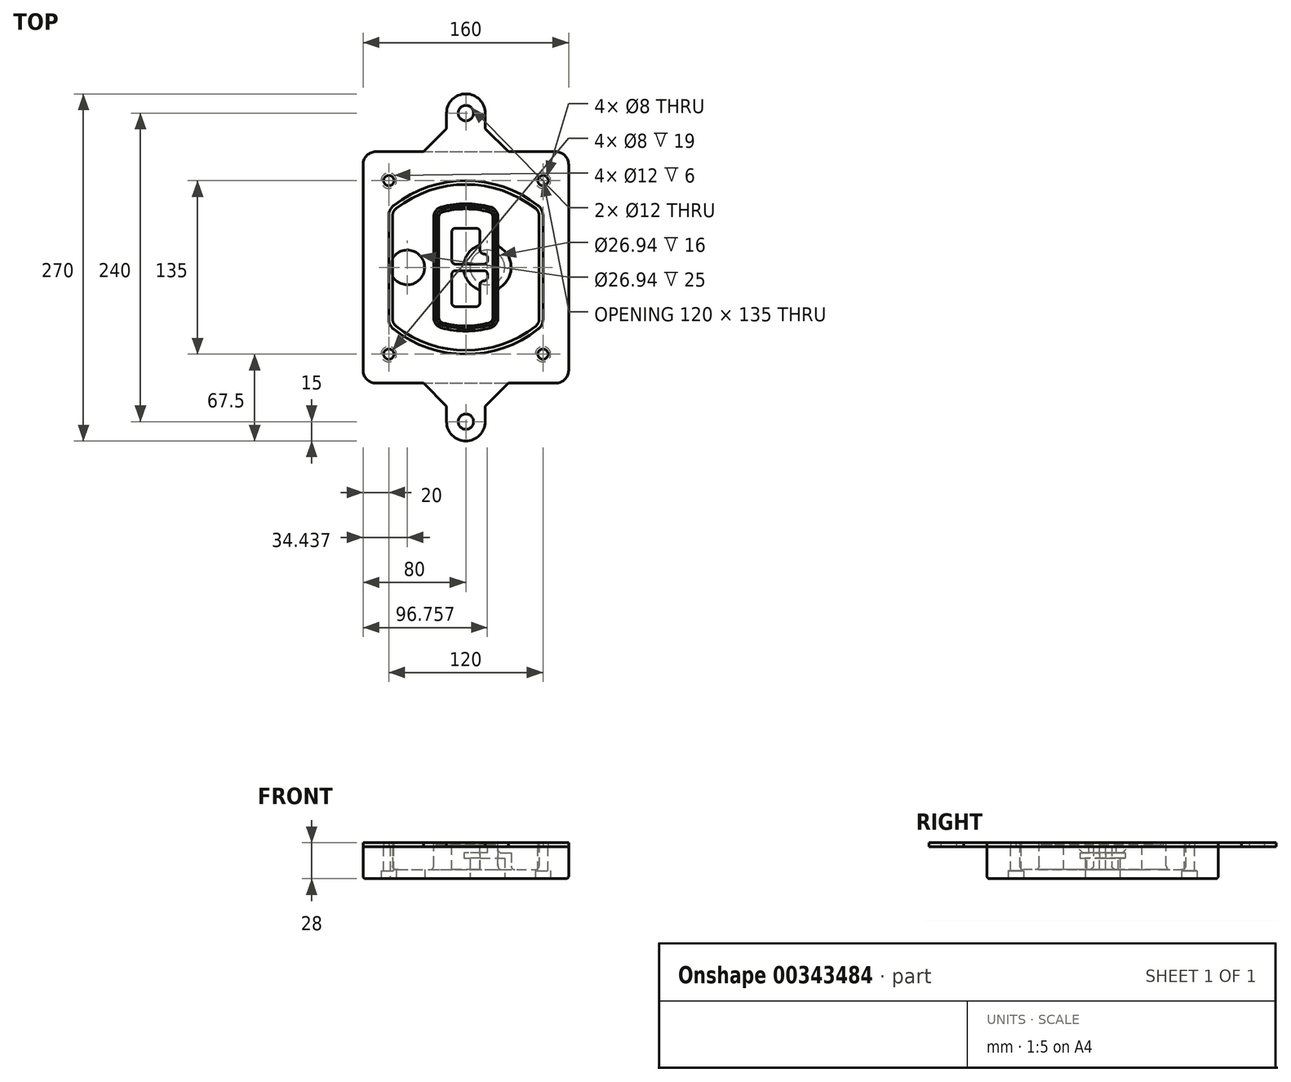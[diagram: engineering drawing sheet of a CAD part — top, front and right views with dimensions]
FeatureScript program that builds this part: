
annotation { "Feature Type Name" : "Feature", "Feature Type Description" : "" }
export const myFeature = defineFeature(function(context is Context, id is Id, definition is map)
    precondition{}
    {
        {
            var Q0;
            Q0=qCreatedBy(makeId("Top.planeOp"),FACE);
            var sketch = newSketch(context, id + "F0", { "sketchPlane" : qUnion([Q0])});
            skPoint(sketch, "E0.rect.middle", {"position": v(0, 0) * mm});
            skLineSegment(sketch, "E1.bottom", {"start": v(-70, -90) * mm, "end": v(70, -90) * mm});
            skLineSegment(sketch, "E1.top", {"start": v(-70, 90) * mm, "end": v(70, 90) * mm});
            skLineSegment(sketch, "E1.left", {"start": v(-80, -80) * mm, "end": v(-80, 80) * mm});
            skLineSegment(sketch, "E1.right", {"start": v(80, -80) * mm, "end": v(80, 80) * mm});
            skLineSegment(sketch, "E2", {"start": v(-80, 90) * mm, "end": v(80, -90) * mm, "construction": true});
            skLineSegment(sketch, "E3", {"start": v(80, 90) * mm, "end": v(-80, -90) * mm, "construction": true});
            skCircle(sketch, "E4", {"center": v(-60, 67.5) * mm, "radius": 4 * mm});
            skCircle(sketch, "E5", {"center": v(60, 67.5) * mm, "radius": 4 * mm});
            skCircle(sketch, "E6", {"center": v(60, -67.5) * mm, "radius": 4 * mm});
            skCircle(sketch, "E7", {"center": v(-60, -67.5) * mm, "radius": 4 * mm});
            skLineSegment(sketch, "E8", {"start": v(-60, 67.5) * mm, "end": v(60, 67.5) * mm, "construction": true});
            skLineSegment(sketch, "E9", {"start": v(60, 67.5) * mm, "end": v(60, -67.5) * mm, "construction": true});
            skLineSegment(sketch, "E10", {"start": v(60, -67.5) * mm, "end": v(-60, -67.5) * mm, "construction": true});
            skLineSegment(sketch, "E11", {"start": v(-60, -67.5) * mm, "end": v(-60, 67.5) * mm, "construction": true});
            skLineSegment(sketch, "E12", {"start": v(-60, 40.3) * mm, "end": v(-60, -40.3) * mm});
            skLineSegment(sketch, "E13", {"start": v(60, 40.3) * mm, "end": v(60, -40.3) * mm});
            skArc(sketch, "E14", {"start": v(56.15, 48.18) * mm, "mid": v(0, 67.5) * mm, "end": v(-56.15, 48.18) * mm});
            skArc(sketch, "E15", {"start": v(-56.15, -48.18) * mm, "mid": v(0, -67.5) * mm, "end": v(56.15, -48.18) * mm});
            skLineSegment(sketch, "E16", {"start": v(-60, 0) * mm, "end": v(60, 0) * mm, "construction": true});
            skPoint(sketch, "E17.visualSharp", {"position": v(-60, -45) * mm});
            skArc(sketch, "E17.filletArc", {"start": v(-60, -40.3) * mm, "mid": v(-58.99, -44.68) * mm, "end": v(-56.15, -48.18) * mm});
            skPoint(sketch, "E18.visualSharp", {"position": v(-60, 45) * mm});
            skArc(sketch, "E18.filletArc", {"start": v(-56.15, 48.18) * mm, "mid": v(-58.99, 44.68) * mm, "end": v(-60, 40.3) * mm});
            skPoint(sketch, "E19.visualSharp", {"position": v(60, 45) * mm});
            skArc(sketch, "E19.filletArc", {"start": v(60, 40.3) * mm, "mid": v(58.99, 44.68) * mm, "end": v(56.15, 48.18) * mm});
            skPoint(sketch, "E20.visualSharp", {"position": v(60, -45) * mm});
            skArc(sketch, "E20.filletArc", {"start": v(56.15, -48.18) * mm, "mid": v(58.99, -44.68) * mm, "end": v(60, -40.3) * mm});
            skPoint(sketch, "E21.visualSharp", {"position": v(-80, 90) * mm});
            skArc(sketch, "E21.filletArc", {"start": v(-70, 90) * mm, "mid": v(-77.07, 87.07) * mm, "end": v(-80, 80) * mm});
            skPoint(sketch, "E22.visualSharp", {"position": v(80, 90) * mm});
            skArc(sketch, "E22.filletArc", {"start": v(80, 80) * mm, "mid": v(77.07, 87.07) * mm, "end": v(70, 90) * mm});
            skPoint(sketch, "E23.visualSharp", {"position": v(80, -90) * mm});
            skArc(sketch, "E23.filletArc", {"start": v(70, -90) * mm, "mid": v(77.07, -87.07) * mm, "end": v(80, -80) * mm});
            skPoint(sketch, "E24.visualSharp", {"position": v(-80, -90) * mm});
            skArc(sketch, "E24.filletArc", {"start": v(-80, -80) * mm, "mid": v(-77.07, -87.07) * mm, "end": v(-70, -90) * mm});
            skArc(sketch, "E25.0", {"start": v(57, 40.3) * mm, "mid": v(56.3, 43.36) * mm, "end": v(54.3, 45.81) * mm});
            skLineSegment(sketch, "E25.1", {"start": v(57, 40.3) * mm, "end": v(57, -40.3) * mm});
            skArc(sketch, "E25.2", {"start": v(54.3, -45.81) * mm, "mid": v(56.3, -43.36) * mm, "end": v(57, -40.3) * mm});
            skArc(sketch, "E25.3", {"start": v(-54.3, -45.81) * mm, "mid": v(0, -64.5) * mm, "end": v(54.3, -45.81) * mm});
            skArc(sketch, "E25.4", {"start": v(-57, -40.3) * mm, "mid": v(-56.3, -43.36) * mm, "end": v(-54.3, -45.81) * mm});
            skArc(sketch, "E25.5", {"start": v(54.3, 45.81) * mm, "mid": v(0, 64.5) * mm, "end": v(-54.3, 45.81) * mm});
            skLineSegment(sketch, "E25.6", {"start": v(-57, 40.3) * mm, "end": v(-57, -40.3) * mm});
            skArc(sketch, "E25.7", {"start": v(-54.3, 45.81) * mm, "mid": v(-56.3, 43.36) * mm, "end": v(-57, 40.3) * mm});
            skArc(sketch, "E26.0", {"start": v(-58.62, 51.33) * mm, "mid": v(-62.58, 46.43) * mm, "end": v(-64, 40.3) * mm});
            skArc(sketch, "E26.1", {"start": v(58.62, 51.33) * mm, "mid": v(0, 71.5) * mm, "end": v(-58.62, 51.33) * mm});
            skArc(sketch, "E26.2", {"start": v(64, 40.3) * mm, "mid": v(62.58, 46.43) * mm, "end": v(58.62, 51.33) * mm});
            skLineSegment(sketch, "E26.3", {"start": v(64, 40.3) * mm, "end": v(64, -40.3) * mm});
            skArc(sketch, "E26.4", {"start": v(58.62, -51.33) * mm, "mid": v(62.58, -46.43) * mm, "end": v(64, -40.3) * mm});
            skLineSegment(sketch, "E26.5", {"start": v(-64, 40.3) * mm, "end": v(-64, -40.3) * mm});
            skArc(sketch, "E26.6", {"start": v(-58.62, -51.33) * mm, "mid": v(0, -71.5) * mm, "end": v(58.62, -51.33) * mm});
            skArc(sketch, "E26.7", {"start": v(-64, -40.3) * mm, "mid": v(-62.58, -46.43) * mm, "end": v(-58.62, -51.33) * mm});
            skSolve(sketch);
        }
        {
            var Q0;
            Q0=makeQuery(id+"F0.imprint","IMPRINT",FACE,{"disambiguationData":[TD([[makeQuery(id+"F0.imprint","IMPRINT",EDGE,{"derivedFrom":sQuery(id+"F0.wireOp",EDGE,"E1.bottom")}),1.0]])]});
            var Q1;
            Q1=makeQuery(id+"F0.imprint","IMPRINT",FACE,{"disambiguationData":[TD([[makeQuery(id+"F0.imprint","IMPRINT",EDGE,{"derivedFrom":sQuery(id+"F0.wireOp",EDGE,"E12")}),1.0]])]});
            var Q2;
            Q2=makeQuery(id+"F0.imprint","IMPRINT",FACE,{"disambiguationData":[TD([[makeQuery(id+"F0.imprint","IMPRINT",EDGE,{"derivedFrom":sQuery(id+"F0.wireOp",EDGE,"E25.0")}),1.0]])]});
            var Q3;
            Q3=makeQuery(id+"F0.imprint","IMPRINT",FACE,{"disambiguationData":[TD([[makeQuery(id+"F0.imprint","IMPRINT",EDGE,{"derivedFrom":sQuery(id+"F0.wireOp",EDGE,"E12")}),-1.0]])]});
            extrude(context, id + "F1", {"entities" : qUnion([Q0, Q1, Q2, Q3]), "oppositeDirection" : true, "depth" : 25 * mm});
        }
        {
            var Q0;
            Q0=makeQuery(id+"F0.imprint","IMPRINT",FACE,{"disambiguationData":[TD([[makeQuery(id+"F0.imprint","IMPRINT",EDGE,{"derivedFrom":sQuery(id+"F0.wireOp",EDGE,"E12")}),1.0]])]});
            extrude(context, id + "F2", {"entities" : qUnion([Q0]), "operationType" : NewBodyOperationType.ADD, "depth" : 3 * mm});
        }
        {
            var Q0;
            Q0=makeQuery(id+"F0.imprint","IMPRINT",FACE,{"disambiguationData":[TD([[makeQuery(id+"F0.imprint","IMPRINT",EDGE,{"derivedFrom":sQuery(id+"F0.wireOp",EDGE,"E25.0")}),1.0]])]});
            extrude(context, id + "F3", {"entities" : qUnion([Q0]), "operationType" : NewBodyOperationType.REMOVE, "oppositeDirection" : true, "depth" : 18 * mm});
        }
        {
            var Q0;
            Q0=makeQuery(id+"F2.opExtrude","CAP_FACE",FACE,{"disambiguationData":[OSD([sQuery(id+"F0.wireOp",EDGE,"E12"),sQuery(id+"F0.wireOp",EDGE,"E13"),sQuery(id+"F0.wireOp",EDGE,"E14"),sQuery(id+"F0.wireOp",EDGE,"E15"),sQuery(id+"F0.wireOp",EDGE,"E17.filletArc"),sQuery(id+"F0.wireOp",EDGE,"E18.filletArc"),sQuery(id+"F0.wireOp",EDGE,"E19.filletArc"),sQuery(id+"F0.wireOp",EDGE,"E20.filletArc"),sQuery(id+"F0.wireOp",EDGE,"E25.0"),sQuery(id+"F0.wireOp",EDGE,"E25.1"),sQuery(id+"F0.wireOp",EDGE,"E25.2"),sQuery(id+"F0.wireOp",EDGE,"E25.3"),sQuery(id+"F0.wireOp",EDGE,"E25.4"),sQuery(id+"F0.wireOp",EDGE,"E25.5"),sQuery(id+"F0.wireOp",EDGE,"E25.6"),sQuery(id+"F0.wireOp",EDGE,"E25.7")])],"isStart":false});
            var sketch = newSketch(context, id + "F4", { "sketchPlane" : qUnion([Q0])});
            skArc(sketch, "E27.0", {"start": v(-19.08, -46.97) * mm, "mid": v(0, -49.5) * mm, "end": v(19.08, -46.97) * mm});
            skArc(sketch, "E28.0", {"start": v(19.08, 46.97) * mm, "mid": v(0, 49.5) * mm, "end": v(-19.08, 46.97) * mm});
            skLineSegment(sketch, "E29", {"start": v(-25, 39.25) * mm, "end": v(-25, -39.25) * mm});
            skLineSegment(sketch, "E30", {"start": v(25, 39.25) * mm, "end": v(25, -39.25) * mm});
            skLineSegment(sketch, "E31", {"start": v(-25, 45.1) * mm, "end": v(25, 45.1) * mm, "construction": true});
            skLineSegment(sketch, "E32", {"start": v(-25, -45.1) * mm, "end": v(25, -45.1) * mm, "construction": true});
            skPoint(sketch, "E33.visualSharp", {"position": v(-25, 45.1) * mm});
            skArc(sketch, "E33.filletArc", {"start": v(-19.08, 46.97) * mm, "mid": v(-23.35, 44.11) * mm, "end": v(-25, 39.25) * mm});
            skPoint(sketch, "E34.visualSharp", {"position": v(25, 45.1) * mm});
            skArc(sketch, "E34.filletArc", {"start": v(25, 39.25) * mm, "mid": v(23.35, 44.11) * mm, "end": v(19.08, 46.97) * mm});
            skPoint(sketch, "E35.visualSharp", {"position": v(25, -45.1) * mm});
            skArc(sketch, "E35.filletArc", {"start": v(19.08, -46.97) * mm, "mid": v(23.35, -44.11) * mm, "end": v(25, -39.25) * mm});
            skPoint(sketch, "E36.visualSharp", {"position": v(-25, -45.1) * mm});
            skArc(sketch, "E36.filletArc", {"start": v(-25, -39.25) * mm, "mid": v(-23.35, -44.11) * mm, "end": v(-19.08, -46.97) * mm});
            skArc(sketch, "E37.0", {"start": v(54.3, 45.81) * mm, "mid": v(0, 64.5) * mm, "end": v(-54.3, 45.81) * mm});
            skArc(sketch, "E37.1", {"start": v(-54.3, 45.81) * mm, "mid": v(-56.3, 43.36) * mm, "end": v(-57, 40.3) * mm});
            skLineSegment(sketch, "E37.2", {"start": v(-57, 40.3) * mm, "end": v(-57, -40.3) * mm});
            skArc(sketch, "E37.3", {"start": v(-57, -40.3) * mm, "mid": v(-56.3, -43.36) * mm, "end": v(-54.3, -45.81) * mm});
            skArc(sketch, "E37.4", {"start": v(-54.3, -45.81) * mm, "mid": v(0, -64.5) * mm, "end": v(54.3, -45.81) * mm});
            skArc(sketch, "E37.5", {"start": v(54.3, -45.81) * mm, "mid": v(56.3, -43.36) * mm, "end": v(57, -40.3) * mm});
            skLineSegment(sketch, "E37.6", {"start": v(57, 40.3) * mm, "end": v(57, -40.3) * mm});
            skArc(sketch, "E37.7", {"start": v(57, 40.3) * mm, "mid": v(56.3, 43.36) * mm, "end": v(54.3, 45.81) * mm});
            skLineSegment(sketch, "E38.0", {"start": v(23, 39.25) * mm, "end": v(23, -39.25) * mm});
            skArc(sketch, "E38.1", {"start": v(18.56, -45.04) * mm, "mid": v(21.76, -42.9) * mm, "end": v(23, -39.25) * mm});
            skArc(sketch, "E38.2", {"start": v(-18.56, -45.04) * mm, "mid": v(0, -47.5) * mm, "end": v(18.56, -45.04) * mm});
            skArc(sketch, "E38.3", {"start": v(-23, -39.25) * mm, "mid": v(-21.76, -42.9) * mm, "end": v(-18.56, -45.04) * mm});
            skLineSegment(sketch, "E38.4", {"start": v(-23, 39.25) * mm, "end": v(-23, -39.25) * mm});
            skArc(sketch, "E38.5", {"start": v(23, 39.25) * mm, "mid": v(21.76, 42.9) * mm, "end": v(18.56, 45.04) * mm});
            skArc(sketch, "E38.6", {"start": v(-18.56, 45.04) * mm, "mid": v(-21.76, 42.9) * mm, "end": v(-23, 39.25) * mm});
            skArc(sketch, "E38.7", {"start": v(18.56, 45.04) * mm, "mid": v(0, 47.5) * mm, "end": v(-18.56, 45.04) * mm});
            skArc(sketch, "E39.0", {"start": v(21, 39.25) * mm, "mid": v(20.18, 41.68) * mm, "end": v(18.04, 43.1) * mm});
            skLineSegment(sketch, "E39.1", {"start": v(21, 39.25) * mm, "end": v(21, -39.25) * mm});
            skArc(sketch, "E39.2", {"start": v(18.04, -43.1) * mm, "mid": v(20.18, -41.68) * mm, "end": v(21, -39.25) * mm});
            skArc(sketch, "E39.3", {"start": v(-18.04, -43.1) * mm, "mid": v(0, -45.5) * mm, "end": v(18.04, -43.1) * mm});
            skArc(sketch, "E39.4", {"start": v(-21, -39.25) * mm, "mid": v(-20.18, -41.68) * mm, "end": v(-18.04, -43.1) * mm});
            skArc(sketch, "E39.5", {"start": v(18.04, 43.1) * mm, "mid": v(0, 45.5) * mm, "end": v(-18.04, 43.1) * mm});
            skLineSegment(sketch, "E39.6", {"start": v(-21, 39.25) * mm, "end": v(-21, -39.25) * mm});
            skArc(sketch, "E39.7", {"start": v(-18.04, 43.1) * mm, "mid": v(-20.18, 41.68) * mm, "end": v(-21, 39.25) * mm});
            skLineSegment(sketch, "E40", {"start": v(-25, 0) * mm, "end": v(25, 0) * mm, "construction": true});
            skLineSegment(sketch, "E41", {"start": v(-11, 5.5) * mm, "end": v(-11, 27.5) * mm});
            skLineSegment(sketch, "E42", {"start": v(-8, 30.5) * mm, "end": v(8, 30.5) * mm});
            skLineSegment(sketch, "E43", {"start": v(11, 27.5) * mm, "end": v(11, 13.5) * mm});
            skLineSegment(sketch, "E44", {"start": v(14, 10.5) * mm, "end": v(14, 10.5) * mm});
            skLineSegment(sketch, "E45", {"start": v(17, 7.5) * mm, "end": v(17, 5.5) * mm});
            skLineSegment(sketch, "E46", {"start": v(14, 2.5) * mm, "end": v(-8, 2.5) * mm});
            skPoint(sketch, "E47.visualSharp", {"position": v(-11, 30.5) * mm});
            skArc(sketch, "E47.filletArc", {"start": v(-8, 30.5) * mm, "mid": v(-10.12, 29.62) * mm, "end": v(-11, 27.5) * mm});
            skPoint(sketch, "E48.visualSharp", {"position": v(11, 30.5) * mm});
            skArc(sketch, "E48.filletArc", {"start": v(11, 27.5) * mm, "mid": v(10.12, 29.62) * mm, "end": v(8, 30.5) * mm});
            skPoint(sketch, "E49.visualSharp", {"position": v(11, 10.5) * mm});
            skArc(sketch, "E49.filletArc", {"start": v(11, 13.5) * mm, "mid": v(11.88, 11.38) * mm, "end": v(14, 10.5) * mm});
            skPoint(sketch, "E50.visualSharp", {"position": v(17, 10.5) * mm});
            skArc(sketch, "E50.filletArc", {"start": v(17, 7.5) * mm, "mid": v(16.12, 9.62) * mm, "end": v(14, 10.5) * mm});
            skPoint(sketch, "E51.visualSharp", {"position": v(17, 2.5) * mm});
            skArc(sketch, "E51.filletArc", {"start": v(14, 2.5) * mm, "mid": v(16.12, 3.38) * mm, "end": v(17, 5.5) * mm});
            skPoint(sketch, "E52.visualSharp", {"position": v(-11, 2.5) * mm});
            skArc(sketch, "E52.filletArc", {"start": v(-11, 5.5) * mm, "mid": v(-10.12, 3.38) * mm, "end": v(-8, 2.5) * mm});
            skLineSegment(sketch, "E53.0.MirrorCS", {"start": v(14, -2.5) * mm, "end": v(-8, -2.5) * mm});
            skArc(sketch, "E54.0.MirrorCS", {"start": v(-11, -5.5) * mm, "mid": v(-10.12, -3.38) * mm, "end": v(-8, -2.5) * mm});
            skLineSegment(sketch, "E55.0.MirrorCS", {"start": v(-11, -5.5) * mm, "end": v(-11, -27.5) * mm});
            skArc(sketch, "E56.0.MirrorCS", {"start": v(-8, -30.5) * mm, "mid": v(-10.12, -29.62) * mm, "end": v(-11, -27.5) * mm});
            skLineSegment(sketch, "E57.0.MirrorCS", {"start": v(-8, -30.5) * mm, "end": v(8, -30.5) * mm});
            skArc(sketch, "E58.0.MirrorCS", {"start": v(11, -27.5) * mm, "mid": v(10.12, -29.62) * mm, "end": v(8, -30.5) * mm});
            skLineSegment(sketch, "E59.0.MirrorCS", {"start": v(11, -27.5) * mm, "end": v(11, -13.5) * mm});
            skArc(sketch, "E60.0.MirrorCS", {"start": v(11, -13.5) * mm, "mid": v(11.88, -11.38) * mm, "end": v(14, -10.5) * mm});
            skArc(sketch, "E61.0.MirrorCS", {"start": v(17, -7.5) * mm, "mid": v(16.12, -9.62) * mm, "end": v(14, -10.5) * mm});
            skLineSegment(sketch, "E62.0.MirrorCS", {"start": v(17, -7.5) * mm, "end": v(17, -5.5) * mm});
            skArc(sketch, "E63.0.MirrorCS", {"start": v(14, -2.5) * mm, "mid": v(16.12, -3.38) * mm, "end": v(17, -5.5) * mm});
            skSolve(sketch);
        }
        {
            var Q0;
            Q0=makeQuery(id+"F4.imprint","IMPRINT",FACE,{"disambiguationData":[TD([[makeQuery(id+"F4.imprint","IMPRINT",EDGE,{"derivedFrom":sQuery(id+"F4.wireOp",EDGE,"E27.0")}),1.0]])]});
            var Q1;
            Q1=makeQuery(id+"F4.imprint","IMPRINT",FACE,{"disambiguationData":[TD([[makeQuery(id+"F4.imprint","IMPRINT",EDGE,{"derivedFrom":sQuery(id+"F4.wireOp",EDGE,"E38.0")}),-1.0]])]});
            var Q2;
            Q2=makeQuery(id+"F4.imprint","IMPRINT",FACE,{"disambiguationData":[TD([[makeQuery(id+"F4.imprint","IMPRINT",EDGE,{"derivedFrom":sQuery(id+"F4.wireOp",EDGE,"E39.0")}),1.0]])]});
            extrude(context, id + "F5", {"entities" : qUnion([Q0, Q1, Q2]), "operationType" : NewBodyOperationType.ADD, "endBound" : BoundingType.UP_TO_NEXT, "oppositeDirection" : true, "depth" : 25 * mm});
        }
        {
            var Q0;
            Q0=makeQuery(id+"F4.imprint","IMPRINT",FACE,{"disambiguationData":[TD([[makeQuery(id+"F4.imprint","IMPRINT",EDGE,{"derivedFrom":sQuery(id+"F4.wireOp",EDGE,"E38.0")}),-1.0]])]});
            extrude(context, id + "F6", {"entities" : qUnion([Q0]), "operationType" : NewBodyOperationType.REMOVE, "oppositeDirection" : true, "depth" : 2 * mm});
        }
        {
            var Q0;
            Q0=makeQuery(id+"F1.opExtrude","CAP_FACE",FACE,{"disambiguationData":[OSD([sQuery(id+"F0.wireOp",EDGE,"E1.bottom"),sQuery(id+"F0.wireOp",EDGE,"E1.top"),sQuery(id+"F0.wireOp",EDGE,"E1.left"),sQuery(id+"F0.wireOp",EDGE,"E1.right"),sQuery(id+"F0.wireOp",EDGE,"E4"),sQuery(id+"F0.wireOp",EDGE,"E5"),sQuery(id+"F0.wireOp",EDGE,"E6"),sQuery(id+"F0.wireOp",EDGE,"E7"),sQuery(id+"F0.wireOp",EDGE,"E21.filletArc"),sQuery(id+"F0.wireOp",EDGE,"E22.filletArc"),sQuery(id+"F0.wireOp",EDGE,"E23.filletArc"),sQuery(id+"F0.wireOp",EDGE,"E24.filletArc")])],"isStart":false});
            var sketch = newSketch(context, id + "F7", { "sketchPlane" : qUnion([Q0])});
            skCircle(sketch, "E64", {"center": v(16.76, 0) * mm, "radius": 13.47 * mm});
            skCircle(sketch, "E65", {"center": v(-45.56, 0) * mm, "radius": 13.47 * mm});
            skLineSegment(sketch, "E66", {"start": v(80, 0) * mm, "end": v(-80, 0) * mm});
            skCircle(sketch, "E67", {"center": v(16.76, 0) * mm, "radius": 18.47 * mm});
            skCircle(sketch, "E68", {"center": v(60, -67.5) * mm, "radius": 6 * mm});
            skCircle(sketch, "E69", {"center": v(-60, -67.5) * mm, "radius": 6 * mm});
            skCircle(sketch, "E70", {"center": v(-60, 67.5) * mm, "radius": 6 * mm});
            skCircle(sketch, "E71", {"center": v(60, 67.5) * mm, "radius": 6 * mm});
            skSolve(sketch);
        }
        {
            var Q0;
            {var subQ1=sQuery(id+"F7.wireOp",EDGE,"E66");var subQ4=sQuery(id+"F7.wireOp",EDGE,"E64");var subQ6=makeQuery(id+"F7.imprint","INTERSECT",VERTEX,{"disambiguationData":[OD(0.0)],"derivedFrom":[subQ4,subQ1]});Q0=makeQuery(id+"F7.imprint","IMPRINT",FACE,{"disambiguationData":[TD([[makeQuery(id+"F7.imprint","IMPRINT",EDGE,{"disambiguationData":[TD([[subQ6,-1.0]])],"derivedFrom":subQ4}),-1.0]])]});}
            var Q1;
            {var subQ0=sQuery(id+"F7.wireOp",EDGE,"E66");var subQ1=sQuery(id+"F7.wireOp",EDGE,"E64");var subQ3=makeQuery(id+"F7.imprint","INTERSECT",VERTEX,{"disambiguationData":[OD(0.0)],"derivedFrom":[subQ1,subQ0]});Q1=makeQuery(id+"F7.imprint","IMPRINT",FACE,{"disambiguationData":[TD([[makeQuery(id+"F7.imprint","IMPRINT",EDGE,{"disambiguationData":[TD([[subQ3,-1.0]])],"derivedFrom":subQ1}),1.0]])]});}
            var Q2;
            {var subQ0=sQuery(id+"F7.wireOp",EDGE,"E66");var subQ1=sQuery(id+"F7.wireOp",EDGE,"E64");var subQ3=makeQuery(id+"F7.imprint","INTERSECT",VERTEX,{"disambiguationData":[OD(0.0)],"derivedFrom":[subQ1,subQ0]});Q2=makeQuery(id+"F7.imprint","IMPRINT",FACE,{"disambiguationData":[TD([[makeQuery(id+"F7.imprint","IMPRINT",EDGE,{"disambiguationData":[TD([[subQ3,1.0]])],"derivedFrom":subQ1}),1.0]])]});}
            var Q3;
            {var subQ1=sQuery(id+"F7.wireOp",EDGE,"E66");var subQ4=sQuery(id+"F7.wireOp",EDGE,"E64");var subQ6=makeQuery(id+"F7.imprint","INTERSECT",VERTEX,{"disambiguationData":[OD(0.0)],"derivedFrom":[subQ4,subQ1]});Q3=makeQuery(id+"F7.imprint","IMPRINT",FACE,{"disambiguationData":[TD([[makeQuery(id+"F7.imprint","IMPRINT",EDGE,{"disambiguationData":[TD([[subQ6,1.0]])],"derivedFrom":subQ4}),-1.0]])]});}
            extrude(context, id + "F8", {"entities" : qUnion([Q0, Q1, Q2, Q3]), "operationType" : NewBodyOperationType.ADD, "oppositeDirection" : true, "depth" : 20 * mm});
        }
        {
            var Q0;
            {var subQ0=sQuery(id+"F7.wireOp",EDGE,"E66");var subQ1=sQuery(id+"F7.wireOp",EDGE,"E64");var subQ3=makeQuery(id+"F7.imprint","INTERSECT",VERTEX,{"disambiguationData":[OD(0.0)],"derivedFrom":[subQ1,subQ0]});Q0=makeQuery(id+"F7.imprint","IMPRINT",FACE,{"disambiguationData":[TD([[makeQuery(id+"F7.imprint","IMPRINT",EDGE,{"disambiguationData":[TD([[subQ3,-1.0]])],"derivedFrom":subQ1}),1.0]])]});}
            var Q1;
            {var subQ0=sQuery(id+"F7.wireOp",EDGE,"E66");var subQ1=sQuery(id+"F7.wireOp",EDGE,"E64");var subQ3=makeQuery(id+"F7.imprint","INTERSECT",VERTEX,{"disambiguationData":[OD(0.0)],"derivedFrom":[subQ1,subQ0]});Q1=makeQuery(id+"F7.imprint","IMPRINT",FACE,{"disambiguationData":[TD([[makeQuery(id+"F7.imprint","IMPRINT",EDGE,{"disambiguationData":[TD([[subQ3,1.0]])],"derivedFrom":subQ1}),1.0]])]});}
            extrude(context, id + "F9", {"entities" : qUnion([Q0, Q1]), "operationType" : NewBodyOperationType.REMOVE, "oppositeDirection" : true, "depth" : 16 * mm});
        }
        {
            var Q0;
            {var subQ0=sQuery(id+"F7.wireOp",EDGE,"E66");var subQ1=sQuery(id+"F7.wireOp",EDGE,"E65");var subQ3=makeQuery(id+"F7.imprint","INTERSECT",VERTEX,{"disambiguationData":[OD(0.0)],"derivedFrom":[subQ1,subQ0]});Q0=makeQuery(id+"F7.imprint","IMPRINT",FACE,{"disambiguationData":[TD([[makeQuery(id+"F7.imprint","IMPRINT",EDGE,{"disambiguationData":[TD([[subQ3,-1.0]])],"derivedFrom":subQ1}),1.0]])]});}
            var Q1;
            {var subQ0=sQuery(id+"F7.wireOp",EDGE,"E66");var subQ1=sQuery(id+"F7.wireOp",EDGE,"E65");var subQ3=makeQuery(id+"F7.imprint","INTERSECT",VERTEX,{"disambiguationData":[OD(0.0)],"derivedFrom":[subQ1,subQ0]});Q1=makeQuery(id+"F7.imprint","IMPRINT",FACE,{"disambiguationData":[TD([[makeQuery(id+"F7.imprint","IMPRINT",EDGE,{"disambiguationData":[TD([[subQ3,1.0]])],"derivedFrom":subQ1}),1.0]])]});}
            extrude(context, id + "F10", {"entities" : qUnion([Q0, Q1]), "operationType" : NewBodyOperationType.REMOVE, "oppositeDirection" : true, "depth" : 25 * mm});
        }
        {
            var Q0;
            Q0=makeQuery(id+"F7.imprint","IMPRINT",FACE,{"disambiguationData":[TD([[makeQuery(id+"F7.imprint","IMPRINT",EDGE,{"derivedFrom":sQuery(id+"F7.wireOp",EDGE,"E68")}),1.0]])]});
            var Q1;
            Q1=makeQuery(id+"F7.imprint","IMPRINT",FACE,{"disambiguationData":[TD([[makeQuery(id+"F7.imprint","IMPRINT",EDGE,{"derivedFrom":makeQuery(id+"F1.opExtrude","CAP_EDGE",EDGE,{"disambiguationData":[OSD([sQuery(id+"F0.wireOp",EDGE,"E5")])],"isStart":false})}),-1.0]])]});
            var Q2;
            Q2=makeQuery(id+"F7.imprint","IMPRINT",FACE,{"disambiguationData":[TD([[makeQuery(id+"F7.imprint","IMPRINT",EDGE,{"derivedFrom":sQuery(id+"F7.wireOp",EDGE,"E69")}),1.0]])]});
            var Q3;
            Q3=makeQuery(id+"F7.imprint","IMPRINT",FACE,{"disambiguationData":[TD([[makeQuery(id+"F7.imprint","IMPRINT",EDGE,{"derivedFrom":makeQuery(id+"F1.opExtrude","CAP_EDGE",EDGE,{"disambiguationData":[OSD([sQuery(id+"F0.wireOp",EDGE,"E4")])],"isStart":false})}),-1.0]])]});
            var Q4;
            Q4=makeQuery(id+"F7.imprint","IMPRINT",FACE,{"disambiguationData":[TD([[makeQuery(id+"F7.imprint","IMPRINT",EDGE,{"derivedFrom":sQuery(id+"F7.wireOp",EDGE,"E70")}),1.0]])]});
            var Q5;
            Q5=makeQuery(id+"F7.imprint","IMPRINT",FACE,{"disambiguationData":[TD([[makeQuery(id+"F7.imprint","IMPRINT",EDGE,{"derivedFrom":makeQuery(id+"F1.opExtrude","CAP_EDGE",EDGE,{"disambiguationData":[OSD([sQuery(id+"F0.wireOp",EDGE,"E7")])],"isStart":false})}),-1.0]])]});
            var Q6;
            Q6=makeQuery(id+"F7.imprint","IMPRINT",FACE,{"disambiguationData":[TD([[makeQuery(id+"F7.imprint","IMPRINT",EDGE,{"derivedFrom":sQuery(id+"F7.wireOp",EDGE,"E71")}),1.0]])]});
            var Q7;
            Q7=makeQuery(id+"F7.imprint","IMPRINT",FACE,{"disambiguationData":[TD([[makeQuery(id+"F7.imprint","IMPRINT",EDGE,{"derivedFrom":makeQuery(id+"F1.opExtrude","CAP_EDGE",EDGE,{"disambiguationData":[OSD([sQuery(id+"F0.wireOp",EDGE,"E6")])],"isStart":false})}),-1.0]])]});
            extrude(context, id + "F11", {"entities" : qUnion([Q0, Q1, Q2, Q3, Q4, Q5, Q6, Q7]), "operationType" : NewBodyOperationType.REMOVE, "oppositeDirection" : true, "depth" : 6 * mm});
        }
        {
            var Q0;
            Q0=makeQuery(id+"F9.boolean.opBoolean","COPY",FACE,{"derivedFrom":makeQuery(id+"F9.opExtrude","CAP_FACE",FACE,{"disambiguationData":[OSD([sQuery(id+"F7.wireOp",EDGE,"E64")])],"isStart":false})});
            var sketch = newSketch(context, id + "F12", { "sketchPlane" : qUnion([Q0])});
            skArc(sketch, "E72.0", {"start": v(11, 17.55) * mm, "mid": v(2.57, 11.82) * mm, "end": v(-1.54, 2.5) * mm});
            skArc(sketch, "E72.1", {"start": v(-1.54, -2.5) * mm, "mid": v(2.57, -11.82) * mm, "end": v(11, -17.55) * mm});
            skLineSegment(sketch, "E73", {"start": v(-1.54, -2.5) * mm, "end": v(14, -2.5) * mm});
            skLineSegment(sketch, "E74.0", {"start": v(14, 2.5) * mm, "end": v(-1.54, 2.5) * mm});
            skArc(sketch, "E74.1", {"start": v(14, 2.5) * mm, "mid": v(16.12, 3.38) * mm, "end": v(17, 5.5) * mm});
            skLineSegment(sketch, "E74.2", {"start": v(17, 7.5) * mm, "end": v(17, 5.5) * mm});
            skArc(sketch, "E74.3", {"start": v(17, 7.5) * mm, "mid": v(16.12, 9.62) * mm, "end": v(14, 10.5) * mm});
            skArc(sketch, "E74.4", {"start": v(11, 13.5) * mm, "mid": v(11.88, 11.38) * mm, "end": v(14, 10.5) * mm});
            skLineSegment(sketch, "E74.5", {"start": v(11, 17.55) * mm, "end": v(11, 13.5) * mm});
            skLineSegment(sketch, "E74.7", {"start": v(14, -2.5) * mm, "end": v(-1.54, -2.5) * mm});
            skArc(sketch, "E74.8", {"start": v(14, -2.5) * mm, "mid": v(16.12, -3.38) * mm, "end": v(17, -5.5) * mm});
            skLineSegment(sketch, "E74.9", {"start": v(17, -7.5) * mm, "end": v(17, -5.5) * mm});
            skArc(sketch, "E74.10", {"start": v(17, -7.5) * mm, "mid": v(16.12, -9.62) * mm, "end": v(14, -10.5) * mm});
            skArc(sketch, "E74.11", {"start": v(11, -13.5) * mm, "mid": v(11.88, -11.38) * mm, "end": v(14, -10.5) * mm});
            skLineSegment(sketch, "E74.12", {"start": v(11, -17.55) * mm, "end": v(11, -13.5) * mm});
            skPoint(sketch, "E75.orphan", {"position": v(11, -27.5) * mm});
            skPoint(sketch, "E76.orphan", {"position": v(-8, -2.5) * mm});
            skPoint(sketch, "E77.orphan", {"position": v(-8, 2.5) * mm});
            skPoint(sketch, "E78.orphan", {"position": v(11, 27.5) * mm});
            skSolve(sketch);
        }
        {
            var Q0;
            {var subQ7=sQuery(id+"F12.wireOp",EDGE,"E72.0");var subQ14=sQuery(id+"F12.wireOp",EDGE,"E72.1");var subQ16=sQuery(id+"F12.wireOp",EDGE,"E74.1");var subQ18=sQuery(id+"F12.wireOp",EDGE,"E74.8");Q0=qUnion([makeQuery(id+"F12.imprint","IMPRINT",FACE,{"disambiguationData":[TD([[makeQuery(id+"F12.imprint","IMPRINT",EDGE,{"derivedFrom":subQ7}),1.0]])]}),makeQuery(id+"F12.imprint","IMPRINT",FACE,{"disambiguationData":[TD([[makeQuery(id+"F12.imprint","IMPRINT",EDGE,{"derivedFrom":subQ14}),1.0]])]}),makeQuery(id+"F12.imprint","IMPRINT",FACE,{"disambiguationData":[TD([[makeQuery(id+"F12.imprint","IMPRINT",EDGE,{"derivedFrom":subQ16}),1.0]])]}),makeQuery(id+"F12.imprint","IMPRINT",FACE,{"disambiguationData":[TD([[makeQuery(id+"F12.imprint","IMPRINT",EDGE,{"derivedFrom":subQ18}),-1.0]])]})]);}
            var Q1;
            Q1=makeQuery(id+"F5.boolean.opBoolean","SPLIT",FACE,{"disambiguationData":[TD([makeQuery(id+"F5.opExtrude","SWEPT_FACE",FACE,{"disambiguationData":[OSD([sQuery(id+"F4.wireOp",EDGE,"E41")])]})])],"derivedFrom":makeQuery(id+"F3.boolean.opBoolean","COPY",FACE,{"derivedFrom":makeQuery(id+"F3.opExtrude","CAP_FACE",FACE,{"disambiguationData":[OSD([sQuery(id+"F0.wireOp",EDGE,"E25.0"),sQuery(id+"F0.wireOp",EDGE,"E25.1"),sQuery(id+"F0.wireOp",EDGE,"E25.2"),sQuery(id+"F0.wireOp",EDGE,"E25.3"),sQuery(id+"F0.wireOp",EDGE,"E25.4"),sQuery(id+"F0.wireOp",EDGE,"E25.5"),sQuery(id+"F0.wireOp",EDGE,"E25.6"),sQuery(id+"F0.wireOp",EDGE,"E25.7")])],"isStart":false})})});
            extrude(context, id + "F13", {"entities" : qUnion([Q0]), "operationType" : NewBodyOperationType.REMOVE, "endBound" : BoundingType.UP_TO_SURFACE, "endBoundEntityFace" : qUnion([Q1]), "depth" : 25 * mm});
        }
        {
            var Q0;
            Q0=makeQuery(id+"F3.boolean.opBoolean","COPY",EDGE,{"derivedFrom":makeQuery(id+"F3.opExtrude","CAP_EDGE",EDGE,{"disambiguationData":[OSD([sQuery(id+"F0.wireOp",EDGE,"E25.6")])],"isStart":false})});
            var Q1;
            Q1=makeQuery(id+"F8.boolean.opBoolean","INTERSECT",EDGE,{"derivedFrom":[makeQuery(id+"F5.opExtrude","SWEPT_FACE",FACE,{"disambiguationData":[OSD([sQuery(id+"F4.wireOp",EDGE,"E30")])]}),makeQuery(id+"F8.opExtrude","CAP_FACE",FACE,{"disambiguationData":[OSD([sQuery(id+"F7.wireOp",EDGE,"E67")])],"isStart":false})]});
            var Q2;
            Q2=makeQuery(id+"F8.boolean.opBoolean","INTERSECT",EDGE,{"disambiguationData":[OD(1.0)],"derivedFrom":[makeQuery(id+"F5.opExtrude","SWEPT_FACE",FACE,{"disambiguationData":[OSD([sQuery(id+"F4.wireOp",EDGE,"E30")])]}),makeQuery(id+"F8.opExtrude","SWEPT_FACE",FACE,{"disambiguationData":[OSD([sQuery(id+"F7.wireOp",EDGE,"E67")])]})]});
            var Q3;
            {var subQ0=sQuery(id+"F4.wireOp",EDGE,"E30");Q3=makeQuery(id+"F8.boolean.opBoolean","SPLIT",EDGE,{"disambiguationData":[TD([makeQuery(id+"F5.opExtrude","SWEPT_FACE",FACE,{"disambiguationData":[OSD([sQuery(id+"F4.wireOp",EDGE,"E35.filletArc")])]})])],"derivedFrom":makeQuery(id+"F5.opExtrude","CAP_EDGE",EDGE,{"disambiguationData":[OSD([subQ0])],"isStart":false})});}
            var Q4;
            {var subQ0=sQuery(id+"F0.wireOp",EDGE,"E25.7");var subQ1=sQuery(id+"F0.wireOp",EDGE,"E25.1");var subQ2=sQuery(id+"F0.wireOp",EDGE,"E25.6");var subQ3=sQuery(id+"F0.wireOp",EDGE,"E25.5");var subQ4=sQuery(id+"F0.wireOp",EDGE,"E25.4");var subQ5=sQuery(id+"F0.wireOp",EDGE,"E25.0");var subQ6=sQuery(id+"F0.wireOp",EDGE,"E25.2");var subQ7=sQuery(id+"F0.wireOp",EDGE,"E25.3");Q4=makeQuery(id+"F8.boolean.opBoolean","INTERSECT",EDGE,{"derivedFrom":[makeQuery(id+"F5.boolean.opBoolean","SPLIT",FACE,{"disambiguationData":[TD([makeQuery(id+"F2.opExtrude","SWEPT_FACE",FACE,{"disambiguationData":[OSD([subQ5])]})])],"derivedFrom":makeQuery(id+"F3.boolean.opBoolean","COPY",FACE,{"derivedFrom":makeQuery(id+"F3.opExtrude","CAP_FACE",FACE,{"disambiguationData":[OSD([subQ5,subQ1,subQ6,subQ7,subQ4,subQ3,subQ2,subQ0])],"isStart":false})})}),makeQuery(id+"F8.opExtrude","SWEPT_FACE",FACE,{"disambiguationData":[OSD([sQuery(id+"F7.wireOp",EDGE,"E67")])]})]});}
            var Q5;
            Q5=makeQuery(id+"F8.boolean.opBoolean","INTERSECT",EDGE,{"disambiguationData":[OD(0.0)],"derivedFrom":[makeQuery(id+"F5.opExtrude","SWEPT_FACE",FACE,{"disambiguationData":[OSD([sQuery(id+"F4.wireOp",EDGE,"E30")])]}),makeQuery(id+"F8.opExtrude","SWEPT_FACE",FACE,{"disambiguationData":[OSD([sQuery(id+"F7.wireOp",EDGE,"E67")])]})]});
            fillet(context, id + "F14", {"entities" : qUnion([Q0, Q1, Q2, Q3, Q4, Q5]), "radius" : 3 * mm, "tangentPropagation" : true, "allowEdgeOverflow" : false});
        }
        {
            var Q0;
            Q0=makeQuery(id+"F1.opExtrude","CAP_EDGE",EDGE,{"disambiguationData":[OSD([sQuery(id+"F0.wireOp",EDGE,"E1.bottom")])],"isStart":false});
            fillet(context, id + "F15", {"entities" : qUnion([Q0]), "radius" : 2 * mm, "tangentPropagation" : true, "allowEdgeOverflow" : false});
        }
        {
            var Q0;
            {var subQ0=sQuery(id+"F0.wireOp",EDGE,"E21.filletArc");var subQ1=sQuery(id+"F0.wireOp",EDGE,"E7");var subQ2=sQuery(id+"F0.wireOp",EDGE,"E6");var subQ3=sQuery(id+"F0.wireOp",EDGE,"E5");var subQ4=sQuery(id+"F0.wireOp",EDGE,"E4");var subQ5=sQuery(id+"F0.wireOp",EDGE,"E22.filletArc");var subQ6=sQuery(id+"F0.wireOp",EDGE,"E1.bottom");var subQ7=sQuery(id+"F0.wireOp",EDGE,"E1.right");var subQ8=sQuery(id+"F0.wireOp",EDGE,"E1.top");var subQ9=sQuery(id+"F0.wireOp",EDGE,"E1.left");var subQ10=sQuery(id+"F0.wireOp",EDGE,"E23.filletArc");var subQ11=sQuery(id+"F0.wireOp",EDGE,"E24.filletArc");Q0=makeQuery(id+"F2.boolean.opBoolean","SPLIT",FACE,{"disambiguationData":[TD([makeQuery(id+"F1.opExtrude","SWEPT_FACE",FACE,{"disambiguationData":[OSD([subQ6])]})])],"derivedFrom":makeQuery(id+"F1.opExtrude","CAP_FACE",FACE,{"disambiguationData":[OSD([subQ6,subQ8,subQ9,subQ7,subQ4,subQ3,subQ2,subQ1,subQ0,subQ5,subQ10,subQ11])],"isStart":true})});}
            var sketch = newSketch(context, id + "F16", { "sketchPlane" : qUnion([Q0])});
            skLineSegment(sketch, "E79.0", {"start": v(-70, 90) * mm, "end": v(70, 90) * mm});
            skArc(sketch, "E79.1", {"start": v(80, 80) * mm, "mid": v(77.07, 87.07) * mm, "end": v(70, 90) * mm});
            skLineSegment(sketch, "E79.2", {"start": v(80, -80) * mm, "end": v(80, 80) * mm});
            skCircle(sketch, "E79.3", {"center": v(60, 67.5) * mm, "radius": 4 * mm});
            skArc(sketch, "E79.4", {"start": v(56.15, 48.18) * mm, "mid": v(0, 67.5) * mm, "end": v(-56.15, 48.18) * mm});
            skArc(sketch, "E79.5", {"start": v(60, 40.3) * mm, "mid": v(58.99, 44.68) * mm, "end": v(56.15, 48.18) * mm});
            skLineSegment(sketch, "E79.6", {"start": v(60, 40.3) * mm, "end": v(60, -40.3) * mm});
            skArc(sketch, "E79.7", {"start": v(-56.15, 48.18) * mm, "mid": v(-58.99, 44.68) * mm, "end": v(-60, 40.3) * mm});
            skLineSegment(sketch, "E79.8", {"start": v(-60, 40.3) * mm, "end": v(-60, -40.3) * mm});
            skLineSegment(sketch, "E79.9", {"start": v(-80, -80) * mm, "end": v(-80, 80) * mm});
            skArc(sketch, "E79.10", {"start": v(-70, 90) * mm, "mid": v(-77.07, 87.07) * mm, "end": v(-80, 80) * mm});
            skCircle(sketch, "E79.11", {"center": v(-60, 67.5) * mm, "radius": 4 * mm});
            skArc(sketch, "E79.12", {"start": v(-60, -40.3) * mm, "mid": v(-58.99, -44.68) * mm, "end": v(-56.15, -48.18) * mm});
            skArc(sketch, "E79.13", {"start": v(-56.15, -48.18) * mm, "mid": v(0, -67.5) * mm, "end": v(56.15, -48.18) * mm});
            skArc(sketch, "E79.14", {"start": v(56.15, -48.18) * mm, "mid": v(58.99, -44.68) * mm, "end": v(60, -40.3) * mm});
            skCircle(sketch, "E79.15", {"center": v(60, -67.5) * mm, "radius": 4 * mm});
            skLineSegment(sketch, "E79.16", {"start": v(-70, -90) * mm, "end": v(70, -90) * mm});
            skArc(sketch, "E79.17", {"start": v(70, -90) * mm, "mid": v(77.07, -87.07) * mm, "end": v(80, -80) * mm});
            skArc(sketch, "E79.18", {"start": v(-80, -80) * mm, "mid": v(-77.07, -87.07) * mm, "end": v(-70, -90) * mm});
            skCircle(sketch, "E79.19", {"center": v(-60, -67.5) * mm, "radius": 4 * mm});
            skLineSegment(sketch, "E80", {"start": v(0, 90) * mm, "end": v(0, 120) * mm, "construction": true});
            skPoint(sketch, "E80.endSnap0", {"position": v(0, 90) * mm});
            skCircle(sketch, "E81", {"center": v(0, 120) * mm, "radius": 6 * mm});
            skLineSegment(sketch, "E82", {"start": v(-33, 90) * mm, "end": v(-15, 108) * mm});
            skLineSegment(sketch, "E83", {"start": v(-15, 108) * mm, "end": v(-15, 120) * mm});
            skArc(sketch, "E84", {"start": v(-15, 120) * mm, "mid": v(0, 135) * mm, "end": v(15, 120) * mm});
            skLineSegment(sketch, "E85", {"start": v(15, 120) * mm, "end": v(15, 108) * mm});
            skLineSegment(sketch, "E86", {"start": v(15, 108) * mm, "end": v(33, 90) * mm});
            skLineSegment(sketch, "E87", {"start": v(-80, 0) * mm, "end": v(80, 0) * mm, "construction": true});
            skLineSegment(sketch, "E88.MirrorCS", {"start": v(-33, -90) * mm, "end": v(-15, -108) * mm});
            skLineSegment(sketch, "E89.MirrorCS", {"start": v(-15, -108) * mm, "end": v(-15, -120) * mm});
            skArc(sketch, "E90.MirrorCS", {"start": v(-15, -120) * mm, "mid": v(0, -135) * mm, "end": v(15, -120) * mm});
            skCircle(sketch, "E91.MirrorC", {"center": v(0, -120) * mm, "radius": 6 * mm});
            skLineSegment(sketch, "E92.MirrorCS", {"start": v(15, -120) * mm, "end": v(15, -108) * mm});
            skLineSegment(sketch, "E93.MirrorCS", {"start": v(15, -108) * mm, "end": v(33, -90) * mm});
            skLineSegment(sketch, "E94.MirrorCS", {"start": v(0, -90) * mm, "end": v(0, -120) * mm, "construction": true});
            skSolve(sketch);
        }
        {
            var Q0;
            Q0=makeQuery(id+"F16.imprint","IMPRINT",FACE,{"disambiguationData":[TD([[makeQuery(id+"F16.imprint","IMPRINT",EDGE,{"derivedFrom":sQuery(id+"F16.wireOp",EDGE,"E81")}),-1.0]])]});
            var Q1;
            {var subQ0=sQuery(id+"F16.wireOp",EDGE,"E88.MirrorCS");Q1=makeQuery(id+"F16.imprint","IMPRINT",FACE,{"disambiguationData":[TD([[makeQuery(id+"F16.imprint","IMPRINT",EDGE,{"derivedFrom":subQ0}),1.0]])]});}
            var Q2;
            {var subQ6=sQuery(id+"F16.wireOp",EDGE,"E79.1");Q2=makeQuery(id+"F16.imprint","IMPRINT",FACE,{"disambiguationData":[TD([[makeQuery(id+"F16.imprint","IMPRINT",EDGE,{"derivedFrom":subQ6}),1.0]])]});}
            var Q3;
            Q3=makeQuery(id+"F2.opExtrude","CAP_FACE",FACE,{"disambiguationData":[OSD([sQuery(id+"F0.wireOp",EDGE,"E12"),sQuery(id+"F0.wireOp",EDGE,"E13"),sQuery(id+"F0.wireOp",EDGE,"E14"),sQuery(id+"F0.wireOp",EDGE,"E15"),sQuery(id+"F0.wireOp",EDGE,"E17.filletArc"),sQuery(id+"F0.wireOp",EDGE,"E18.filletArc"),sQuery(id+"F0.wireOp",EDGE,"E19.filletArc"),sQuery(id+"F0.wireOp",EDGE,"E20.filletArc"),sQuery(id+"F0.wireOp",EDGE,"E25.0"),sQuery(id+"F0.wireOp",EDGE,"E25.1"),sQuery(id+"F0.wireOp",EDGE,"E25.2"),sQuery(id+"F0.wireOp",EDGE,"E25.3"),sQuery(id+"F0.wireOp",EDGE,"E25.4"),sQuery(id+"F0.wireOp",EDGE,"E25.5"),sQuery(id+"F0.wireOp",EDGE,"E25.6"),sQuery(id+"F0.wireOp",EDGE,"E25.7")])],"isStart":false});
            extrude(context, id + "F17", {"entities" : qUnion([Q0, Q1, Q2]), "endBound" : BoundingType.UP_TO_SURFACE, "endBoundEntityFace" : qUnion([Q3]), "depth" : 25 * mm});
        }
    });
